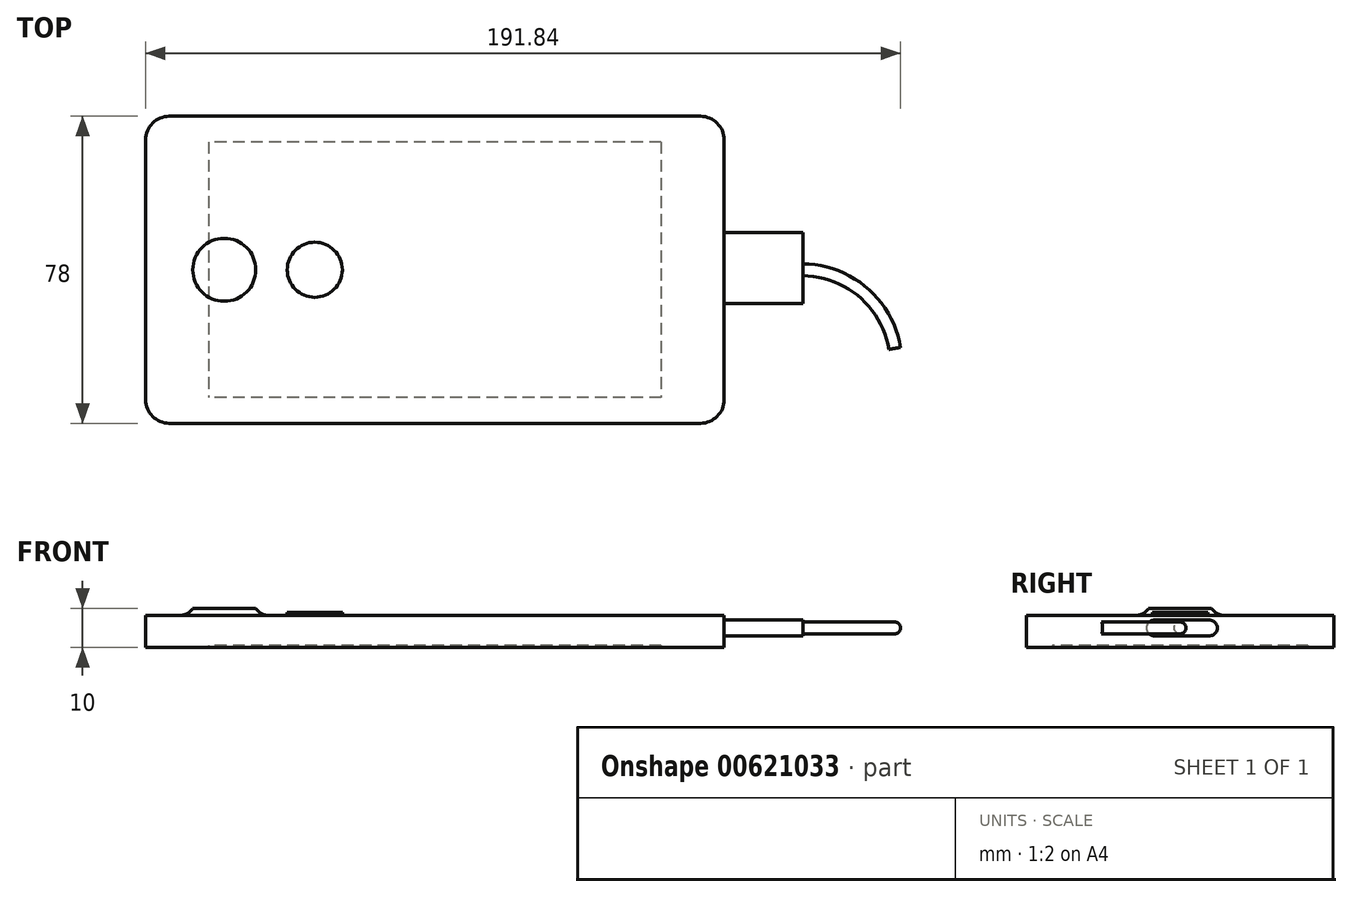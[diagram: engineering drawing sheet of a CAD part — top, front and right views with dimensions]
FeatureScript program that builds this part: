
annotation { "Feature Type Name" : "Feature", "Feature Type Description" : "" }
export const myFeature = defineFeature(function(context is Context, id is Id, definition is map)
    precondition{}
    {
        {
            var Q0;
            Q0=qCreatedBy(makeId("Top.planeOp"),FACE);
            var sketch = newSketch(context, id + "F0", { "sketchPlane" : qUnion([Q0])});
            skLineSegment(sketch, "E0.bottom", {"start": v(67.5, -39) * mm, "end": v(-67.5, -39) * mm});
            skLineSegment(sketch, "E0.top", {"start": v(67.5, 39) * mm, "end": v(-67.5, 39) * mm});
            skLineSegment(sketch, "E0.left", {"start": v(73.5, -33) * mm, "end": v(73.5, 33) * mm});
            skLineSegment(sketch, "E0.right", {"start": v(-73.5, -33) * mm, "end": v(-73.5, 33) * mm});
            skPoint(sketch, "E0.middle", {"position": v(0, 0) * mm});
            skPoint(sketch, "E1.visualSharp", {"position": v(-73.5, 39) * mm});
            skArc(sketch, "E1.filletArc", {"start": v(-67.5, 39) * mm, "mid": v(-71.74, 37.24) * mm, "end": v(-73.5, 33) * mm});
            skPoint(sketch, "E2.visualSharp", {"position": v(73.5, 39) * mm});
            skArc(sketch, "E2.filletArc", {"start": v(73.5, 33) * mm, "mid": v(71.74, 37.24) * mm, "end": v(67.5, 39) * mm});
            skPoint(sketch, "E3.visualSharp", {"position": v(73.5, -39) * mm});
            skArc(sketch, "E3.filletArc", {"start": v(67.5, -39) * mm, "mid": v(71.74, -37.24) * mm, "end": v(73.5, -33) * mm});
            skPoint(sketch, "E4.visualSharp", {"position": v(-73.5, -39) * mm});
            skArc(sketch, "E4.filletArc", {"start": v(-73.5, -33) * mm, "mid": v(-71.74, -37.24) * mm, "end": v(-67.5, -39) * mm});
            skCircle(sketch, "E5", {"center": v(-53.5, 0) * mm, "radius": 8 * mm});
            skCircle(sketch, "E6", {"center": v(-30.5, 0) * mm, "radius": 7 * mm});
            skSolve(sketch);
        }
        {
            var Q0;
            Q0=makeQuery(id+"F0.imprint","IMPRINT",FACE,{"disambiguationData":[TD([[makeQuery(id+"F0.imprint","IMPRINT",EDGE,{"derivedFrom":sQuery(id+"F0.wireOp",EDGE,"E5")}),1.0]])]});
            var Q1;
            Q1=makeQuery(id+"F0.imprint","IMPRINT",FACE,{"disambiguationData":[TD([[makeQuery(id+"F0.imprint","IMPRINT",EDGE,{"derivedFrom":sQuery(id+"F0.wireOp",EDGE,"E0.bottom")}),-1.0]])]});
            var Q2;
            Q2=makeQuery(id+"F0.imprint","IMPRINT",FACE,{"disambiguationData":[TD([[makeQuery(id+"F0.imprint","IMPRINT",EDGE,{"derivedFrom":sQuery(id+"F0.wireOp",EDGE,"E6")}),1.0]])]});
            extrude(context, id + "F1", {"entities" : qUnion([Q0, Q1, Q2]), "depth" : 8.15 * mm, "offsetDistance" : 25 * mm});
        }
        {
            var Q0;
            Q0=makeQuery(id+"F0.imprint","IMPRINT",FACE,{"disambiguationData":[TD([[makeQuery(id+"F0.imprint","IMPRINT",EDGE,{"derivedFrom":sQuery(id+"F0.wireOp",EDGE,"E5")}),1.0]])]});
            extrude(context, id + "F2", {"entities" : qUnion([Q0]), "operationType" : NewBodyOperationType.ADD, "depth" : 10 * mm, "offsetDistance" : 25 * mm});
        }
        {
            var Q0;
            Q0=makeQuery(id+"F0.imprint","IMPRINT",FACE,{"disambiguationData":[TD([[makeQuery(id+"F0.imprint","IMPRINT",EDGE,{"derivedFrom":sQuery(id+"F0.wireOp",EDGE,"E6")}),1.0]])]});
            extrude(context, id + "F3", {"entities" : qUnion([Q0]), "operationType" : NewBodyOperationType.ADD, "depth" : 9 * mm, "offsetDistance" : 25 * mm});
        }
        {
            var Q0;
            Q0=makeQuery(id+"F2.boolean.opBoolean","INTERSECT",EDGE,{"derivedFrom":[makeQuery(id+"F1.opExtrude","CAP_FACE",FACE,{"disambiguationData":[OSD([sQuery(id+"F0.wireOp",EDGE,"E0.bottom"),sQuery(id+"F0.wireOp",EDGE,"E0.top"),sQuery(id+"F0.wireOp",EDGE,"E0.left"),sQuery(id+"F0.wireOp",EDGE,"E0.right"),sQuery(id+"F0.wireOp",EDGE,"E1.filletArc"),sQuery(id+"F0.wireOp",EDGE,"E2.filletArc"),sQuery(id+"F0.wireOp",EDGE,"E3.filletArc"),sQuery(id+"F0.wireOp",EDGE,"E4.filletArc")])],"isStart":false}),makeQuery(id+"F2.opExtrude","SWEPT_FACE",FACE,{"disambiguationData":[OSD([sQuery(id+"F0.wireOp",EDGE,"E5")])]})]});
            fillet(context, id + "F4", {"entities" : qUnion([Q0]), "radius" : 4 * mm, "tangentPropagation" : true, "allowEdgeOverflow" : false});
        }
        {
            var Q0;
            Q0=qCreatedBy(makeId("Top.planeOp"),FACE);
            var sketch = newSketch(context, id + "F5", { "sketchPlane" : qUnion([Q0])});
            skLineSegment(sketch, "E7.bottom", {"start": v(57.5, 32.5) * mm, "end": v(-57.5, 32.5) * mm});
            skLineSegment(sketch, "E7.top", {"start": v(57.5, -32.5) * mm, "end": v(-57.5, -32.5) * mm});
            skLineSegment(sketch, "E7.left", {"start": v(57.5, 32.5) * mm, "end": v(57.5, -32.5) * mm});
            skLineSegment(sketch, "E7.right", {"start": v(-57.5, 32.5) * mm, "end": v(-57.5, -32.5) * mm});
            skPoint(sketch, "E7.middle", {"position": v(0, 0) * mm});
            skSolve(sketch);
        }
        {
            var Q0;
            Q0=makeQuery(id+"F5.imprint","IMPRINT",FACE,{"disambiguationData":[TD([[makeQuery(id+"F5.imprint","IMPRINT",EDGE,{"derivedFrom":sQuery(id+"F5.wireOp",EDGE,"E7.bottom")}),1.0]])]});
            extrude(context, id + "F6", {"entities" : qUnion([Q0]), "operationType" : NewBodyOperationType.REMOVE, "depth" : 0.5 * mm, "offsetDistance" : 25 * mm});
        }
        {
            var Q0;
            Q0=makeQuery(id+"F1.opExtrude","SWEPT_FACE",FACE,{"disambiguationData":[OSD([sQuery(id+"F0.wireOp",EDGE,"E0.left")])]});
            var sketch = newSketch(context, id + "F7", { "sketchPlane" : qUnion([Q0])});
            skLineSegment(sketch, "E8", {"start": v(7.45, 5) * mm, "end": v(-6.55, 5) * mm});
            skArc(sketch, "E9.0.startCap", {"start": v(7.45, 7) * mm, "mid": v(9.45, 5) * mm, "end": v(7.45, 3) * mm});
            skArc(sketch, "E9.0.endCap", {"start": v(-6.55, 3) * mm, "mid": v(-8.55, 5) * mm, "end": v(-6.55, 7) * mm});
            skLineSegment(sketch, "E9.0.left", {"start": v(7.45, 3) * mm, "end": v(-6.55, 3) * mm});
            skLineSegment(sketch, "E9.0.right", {"start": v(7.45, 7) * mm, "end": v(-6.55, 7) * mm});
            skCircle(sketch, "E10", {"center": v(0, 5) * mm, "radius": 1.5 * mm});
            skSolve(sketch);
        }
        {
            var Q0;
            Q0 = qSketchRegion(id + "F7", true);
            var Q1;
            {var subQ0=sQuery(id+"F7.wireOp",EDGE,"E10");var subQ1=sQuery(id+"F7.wireOp",EDGE,"E8");var subQ2=makeQuery(id+"F7.imprint","INTERSECT",VERTEX,{"disambiguationData":[OD(0.0)],"derivedFrom":[subQ1,subQ0]});Q1=makeQuery(id+"F7.imprint","IMPRINT",FACE,{"disambiguationData":[TD([[makeQuery(id+"F7.imprint","IMPRINT",EDGE,{"disambiguationData":[TD([[subQ2,1.0]])],"derivedFrom":subQ1}),-1.0]])]});}
            var Q2;
            {var subQ0=sQuery(id+"F7.wireOp",EDGE,"E10");var subQ1=sQuery(id+"F7.wireOp",EDGE,"E8");var subQ2=makeQuery(id+"F7.imprint","INTERSECT",VERTEX,{"disambiguationData":[OD(0.0)],"derivedFrom":[subQ1,subQ0]});Q2=makeQuery(id+"F7.imprint","IMPRINT",FACE,{"disambiguationData":[TD([[makeQuery(id+"F7.imprint","IMPRINT",EDGE,{"disambiguationData":[TD([[subQ2,1.0]])],"derivedFrom":subQ1}),1.0]])]});}
            extrude(context, id + "F8", {"entities" : qUnion([Q0, Q1, Q2]), "operationType" : NewBodyOperationType.ADD, "depth" : 20 * mm, "offsetDistance" : 25 * mm});
        }
        {
            var Q0;
            Q0=makeQuery(id+"F8.opExtrude","SWEPT_FACE",FACE,{"disambiguationData":[OSD([sQuery(id+"F7.wireOp",EDGE,"E9.0.left")])]});
            cPlane(context, id + "F9", {"entities" : qUnion([Q0]), "cplaneType" : CPlaneType.OFFSET, "offset" : 2 * mm, "oppositeDirection" : true, "width" : 150 * mm, "height" : 150 * mm});
        }
        {
            var Q0;
            Q0=qCreatedBy(id+"F9.planeOp",FACE);
            var sketch = newSketch(context, id + "F10", { "sketchPlane" : qUnion([Q0])});
            skArc(sketch, "E11", {"start": v(93.5, 0) * mm, "mid": v(108.81, 5.74) * mm, "end": v(116.86, 19.97) * mm});
            skLineSegment(sketch, "E12.0", {"start": v(93.5, -7.45) * mm, "end": v(93.5, 6.55) * mm});
            skSolve(sketch);
        }
        {
            var Q0;
            Q0=makeQuery(id+"F8.opExtrude","CAP_FACE",FACE,{"disambiguationData":[OSD([sQuery(id+"F7.wireOp",EDGE,"E8"),sQuery(id+"F7.wireOp",EDGE,"E9.0.startCap"),sQuery(id+"F7.wireOp",EDGE,"E9.0.endCap"),sQuery(id+"F7.wireOp",EDGE,"E9.0.left"),sQuery(id+"F7.wireOp",EDGE,"E9.0.right"),sQuery(id+"F7.wireOp",EDGE,"E10")])],"isStart":false});
            var sketch = newSketch(context, id + "F11", { "sketchPlane" : qUnion([Q0])});
            skCircle(sketch, "E13.0", {"center": v(0, 5) * mm, "radius": 1.5 * mm});
            skSolve(sketch);
        }
        {
            var Q0;
            Q0=makeQuery(id+"F11.imprint","IMPRINT",FACE,{"disambiguationData":[TD([[makeQuery(id+"F11.imprint","IMPRINT",EDGE,{"derivedFrom":sQuery(id+"F11.wireOp",EDGE,"E13.0")}),1.0]])]});
            var Q1;
            Q1=sQuery(id+"F10.wireOp",EDGE,"E11");
            sweep(context, id + "F12", {"operationType" : NewBodyOperationType.ADD, "profiles" : qUnion([Q0]), "path" : qUnion([Q1])});
        }
    });
